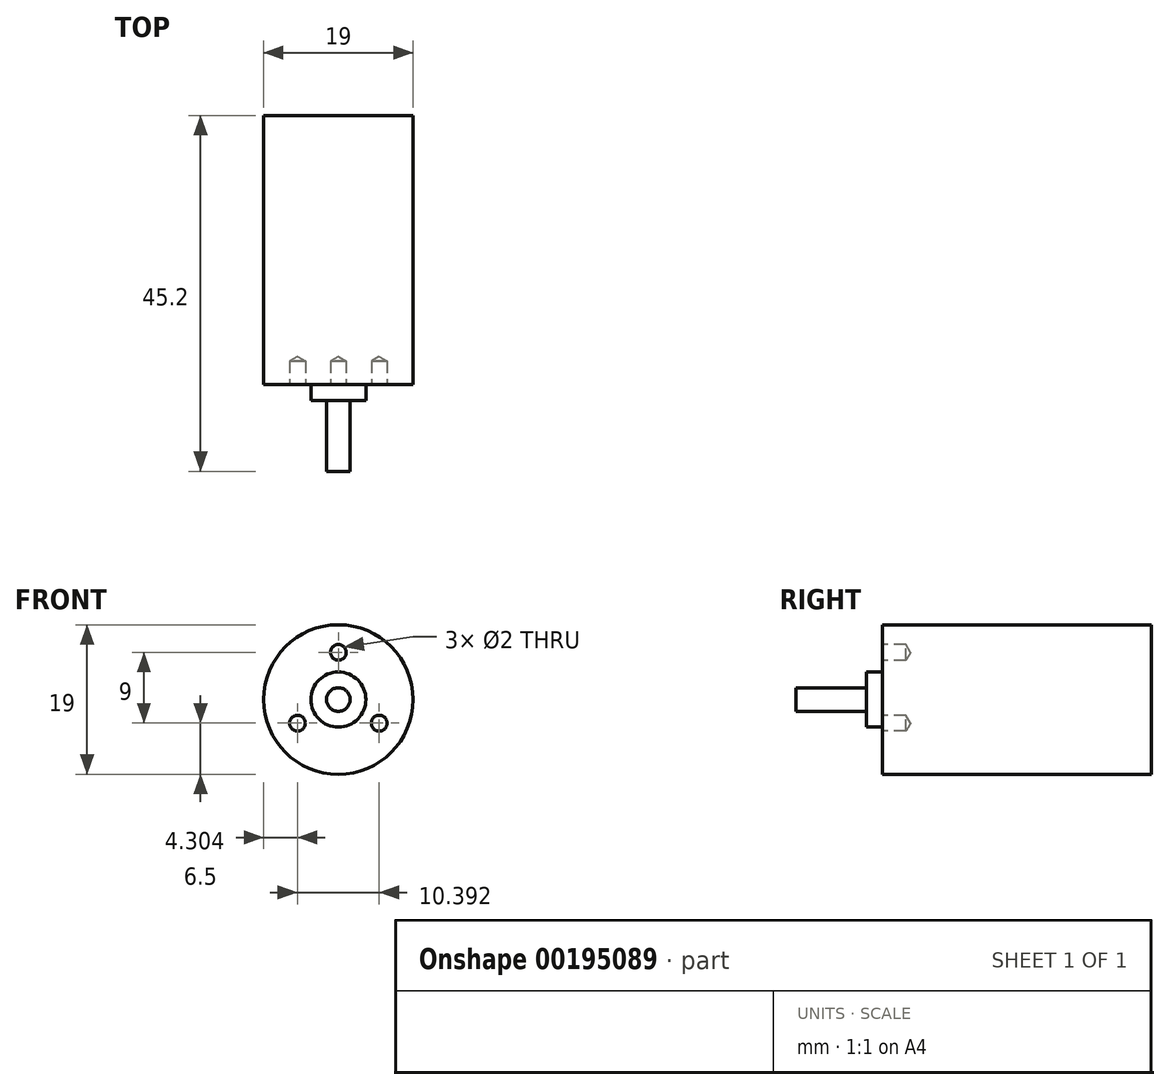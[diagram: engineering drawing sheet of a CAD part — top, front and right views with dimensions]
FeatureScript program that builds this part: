
annotation { "Feature Type Name" : "Feature", "Feature Type Description" : "" }
export const myFeature = defineFeature(function(context is Context, id is Id, definition is map)
    precondition{}
    {
        {
            var Q0;
            Q0=qCreatedBy(makeId("Front.planeOp"),FACE);
            var sketch = newSketch(context, id + "F0", { "sketchPlane" : qUnion([Q0])});
            skCircle(sketch, "E0", {"center": v(0, 0) * mm, "radius": 9.5 * mm});
            skSolve(sketch);
        }
        {
            var Q0;
            Q0=makeQuery(id+"F0.imprint","IMPRINT",FACE,{"disambiguationData":[TD([[makeQuery(id+"F0.imprint","IMPRINT",EDGE,{"derivedFrom":sQuery(id+"F0.wireOp",EDGE,"E0")}),1.0]])]});
            extrude(context, id + "F1", {"entities" : qUnion([Q0]), "depth" : 34.2 * mm});
        }
        {
            var Q0;
            Q0=makeQuery(id+"F1.opExtrude","CAP_FACE",FACE,{"disambiguationData":[OSD([sQuery(id+"F0.wireOp",EDGE,"E0")])],"isStart":false});
            var sketch = newSketch(context, id + "F2", { "sketchPlane" : qUnion([Q0])});
            skCircle(sketch, "E1", {"center": v(0, 0) * mm, "radius": 3.5 * mm});
            skSolve(sketch);
        }
        {
            var Q0;
            Q0=makeQuery(id+"F2.imprint","IMPRINT",FACE,{"disambiguationData":[TD([[makeQuery(id+"F2.imprint","IMPRINT",EDGE,{"derivedFrom":sQuery(id+"F2.wireOp",EDGE,"E1")}),1.0]])]});
            extrude(context, id + "F3", {"entities" : qUnion([Q0]), "operationType" : NewBodyOperationType.ADD, "depth" : 2 * mm});
        }
        {
            var Q0;
            Q0=makeQuery(id+"F3.opExtrude","CAP_FACE",FACE,{"disambiguationData":[OSD([sQuery(id+"F2.wireOp",EDGE,"E1")])],"isStart":false});
            var sketch = newSketch(context, id + "F4", { "sketchPlane" : qUnion([Q0])});
            skCircle(sketch, "E2", {"center": v(0, 0) * mm, "radius": 1.5 * mm});
            skSolve(sketch);
        }
        {
            var Q0;
            Q0=makeQuery(id+"F4.imprint","IMPRINT",FACE,{"disambiguationData":[TD([[makeQuery(id+"F4.imprint","IMPRINT",EDGE,{"derivedFrom":sQuery(id+"F4.wireOp",EDGE,"E2")}),1.0]])]});
            extrude(context, id + "F5", {"entities" : qUnion([Q0]), "operationType" : NewBodyOperationType.ADD, "depth" : 9 * mm});
        }
        {
            var Q0;
            Q0=makeQuery(id+"F1.opExtrude","CAP_FACE",FACE,{"disambiguationData":[OSD([sQuery(id+"F0.wireOp",EDGE,"E0")])],"isStart":false});
            var sketch = newSketch(context, id + "F6", { "sketchPlane" : qUnion([Q0])});
            skLineSegment(sketch, "E3", {"start": v(0, 0) * mm, "end": v(0, 17.1) * mm, "construction": true});
            skLineSegment(sketch, "E4", {"start": v(0, 0) * mm, "end": v(16.07, -9.28) * mm});
            skLineSegment(sketch, "E5", {"start": v(16.07, -9.28) * mm, "end": v(0, 0) * mm, "construction": true});
            skLineSegment(sketch, "E6", {"start": v(0, 0) * mm, "end": v(-14.6, -8.43) * mm, "construction": true});
            skCircle(sketch, "E7", {"center": v(0, 0) * mm, "radius": 6 * mm, "construction": true});
            skPoint(sketch, "E8", {"position": v(0, 6) * mm});
            skPoint(sketch, "E9", {"position": v(5.2, -3) * mm});
            skPoint(sketch, "E10", {"position": v(-5.2, -3) * mm});
            skSolve(sketch);
        }
        {
            var Q0;
            Q0=sQuery(id+"F6.wireOp",VERTEX,"E8");
            var Q1;
            Q1=sQuery(id+"F6.wireOp",VERTEX,"E10");
            var Q2;
            Q2=sQuery(id+"F6.wireOp",VERTEX,"E9");
            var Q3;
            Q3=makeQuery(id+"F1.opExtrude","SWEPT_BODY",BODY,{"disambiguationData":[OSD([sQuery(id+"F0.wireOp",EDGE,"E0")])]});
            hole(context, id + "F7", {"style" : HoleStyle.SIMPLE, "endStyle" : HoleEndStyle.BLIND, "standardTappedOrClearance" : lookupTablePath({ "standard" : "ISO", "size" : "2", "type" : "Drilled" }), "standardBlindInLast" : lookupTablePath({ "standard" : "ISO", "size" : "2", "type" : "Drilled" }), "holeDiameter" : 2 * mm, "holeDepth" : 3 * mm, "locations" : qUnion([Q0, Q1, Q2]), "scope" : qUnion([Q3])});
        }
    });
